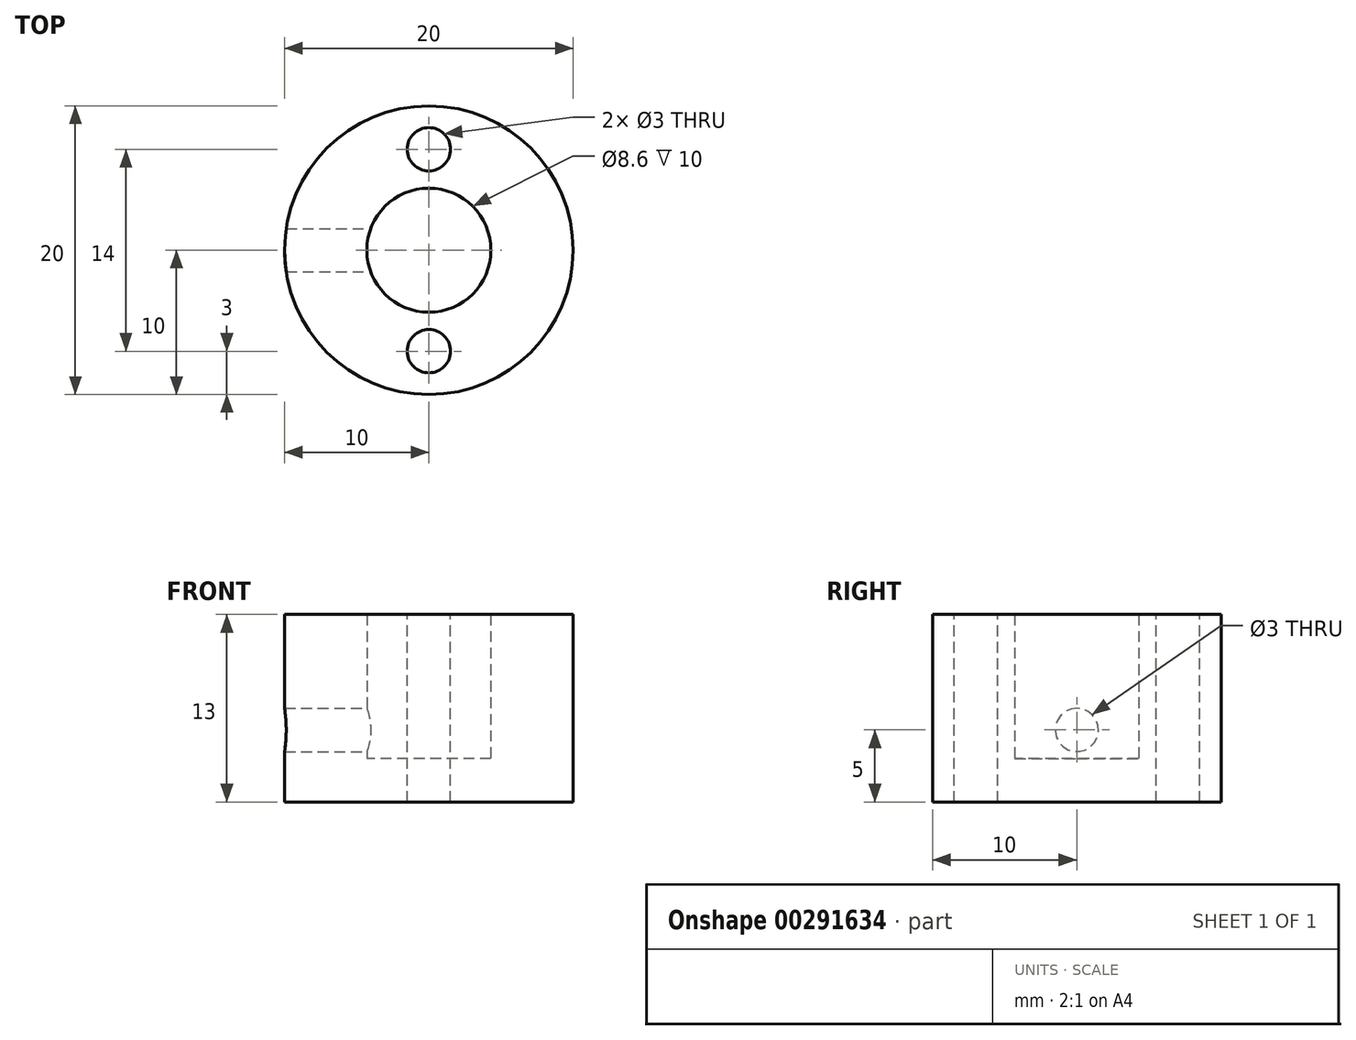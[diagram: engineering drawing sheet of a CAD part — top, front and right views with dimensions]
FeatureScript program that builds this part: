
annotation { "Feature Type Name" : "Feature", "Feature Type Description" : "" }
export const myFeature = defineFeature(function(context is Context, id is Id, definition is map)
    precondition{}
    {
        {
            var Q0;
            Q0=qCreatedBy(makeId("Top.planeOp"),FACE);
            var sketch = newSketch(context, id + "F0", { "sketchPlane" : qUnion([Q0])});
            skCircle(sketch, "E0", {"center": v(0, 0) * mm, "radius": 10 * mm});
            skCircle(sketch, "E1", {"center": v(0, 0) * mm, "radius": 4.3 * mm});
            skSolve(sketch);
        }
        {
            var Q0;
            Q0=makeQuery(id+"F0.imprint","IMPRINT",FACE,{"disambiguationData":[TD([[makeQuery(id+"F0.imprint","IMPRINT",EDGE,{"derivedFrom":sQuery(id+"F0.wireOp",EDGE,"E0")}),1.0]])]});
            extrude(context, id + "F1", {"entities" : qUnion([Q0]), "depth" : 13 * mm});
        }
        {
            var Q0;
            Q0=qCreatedBy(makeId("Top.planeOp"),FACE);
            var sketch = newSketch(context, id + "F2", { "sketchPlane" : qUnion([Q0])});
            skCircle(sketch, "E2", {"center": v(0, 0) * mm, "radius": 4.3 * mm});
            skSolve(sketch);
        }
        {
            var Q0;
            Q0 = qSketchRegion(id + "F2", true);
            extrude(context, id + "F3", {"entities" : qUnion([Q0]), "operationType" : NewBodyOperationType.ADD, "depth" : 3 * mm});
        }
        {
            var Q0;
            Q0=makeQuery(id+"F1.opExtrude","CAP_FACE",FACE,{"disambiguationData":[OSD([sQuery(id+"F0.wireOp",EDGE,"E0"),sQuery(id+"F0.wireOp",EDGE,"E1")])],"isStart":false});
            cPlane(context, id + "F4", {"entities" : qUnion([Q0]), "cplaneType" : CPlaneType.OFFSET, "offset" : 0 * mm, "width" : 152.4 * mm, "height" : 152.4 * mm});
        }
        {
            var Q0;
            Q0=qCreatedBy(id+"F4.planeOp",FACE);
            var sketch = newSketch(context, id + "F5", { "sketchPlane" : qUnion([Q0])});
            skLineSegment(sketch, "E3", {"start": v(0, -8.95) * mm, "end": v(0, 10.71) * mm});
            skLineSegment(sketch, "E4", {"start": v(-12.79, 0) * mm, "end": v(12.24, 0) * mm});
            skCircle(sketch, "E5", {"center": v(0, 7) * mm, "radius": 1.5 * mm});
            skCircle(sketch, "E6.MirrorC", {"center": v(0, -7) * mm, "radius": 1.5 * mm});
            skSolve(sketch);
        }
        {
            var Q0;
            Q0 = qSketchRegion(id + "F5", true);
            extrude(context, id + "F6", {"entities" : qUnion([Q0]), "operationType" : NewBodyOperationType.REMOVE, "oppositeDirection" : true, "depth" : 25.4 * mm});
        }
        {
            var Q0;
            Q0=qCreatedBy(makeId("Right.planeOp"),FACE);
            var sketch = newSketch(context, id + "F7", { "sketchPlane" : qUnion([Q0])});
            skCircle(sketch, "E7", {"center": v(0, 5) * mm, "radius": 1.5 * mm});
            skSolve(sketch);
        }
        {
            var Q0;
            Q0 = qSketchRegion(id + "F7", true);
            extrude(context, id + "F8", {"entities" : qUnion([Q0]), "operationType" : NewBodyOperationType.REMOVE, "oppositeDirection" : true, "depth" : 25.4 * mm});
        }
    });
